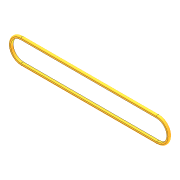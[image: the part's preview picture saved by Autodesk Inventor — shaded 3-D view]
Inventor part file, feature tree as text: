
AUTODESK INVENTOR PART (.ipt)
format: ipt  version: 2012 (Build 160160000, 160)  size: 94,208 bytes
history: native  units: in
note: dims shown in document units (in); Inventor stores cm internally (conversion verified against a paired STEP export)
features: extrude x1, fillet x1, sketch x1
ambient origin geometry x8: Origin, YZ Plane, XZ Plane, XY Plane, X Axis, Y Axis, Z Axis, Center Point
bodies: Solid1 (feature_tree)
feature tree (3):
  extrude  "Extrusion1"  Depth=10.0in
  fillet  "Fillet1"  Radius=0.1875in
  sketch  "Sketch1"  dims[d0=0.75in d1=10.0in d2=0.1875in d3=0.1875in d4=0.0in d5=0.0938in]
